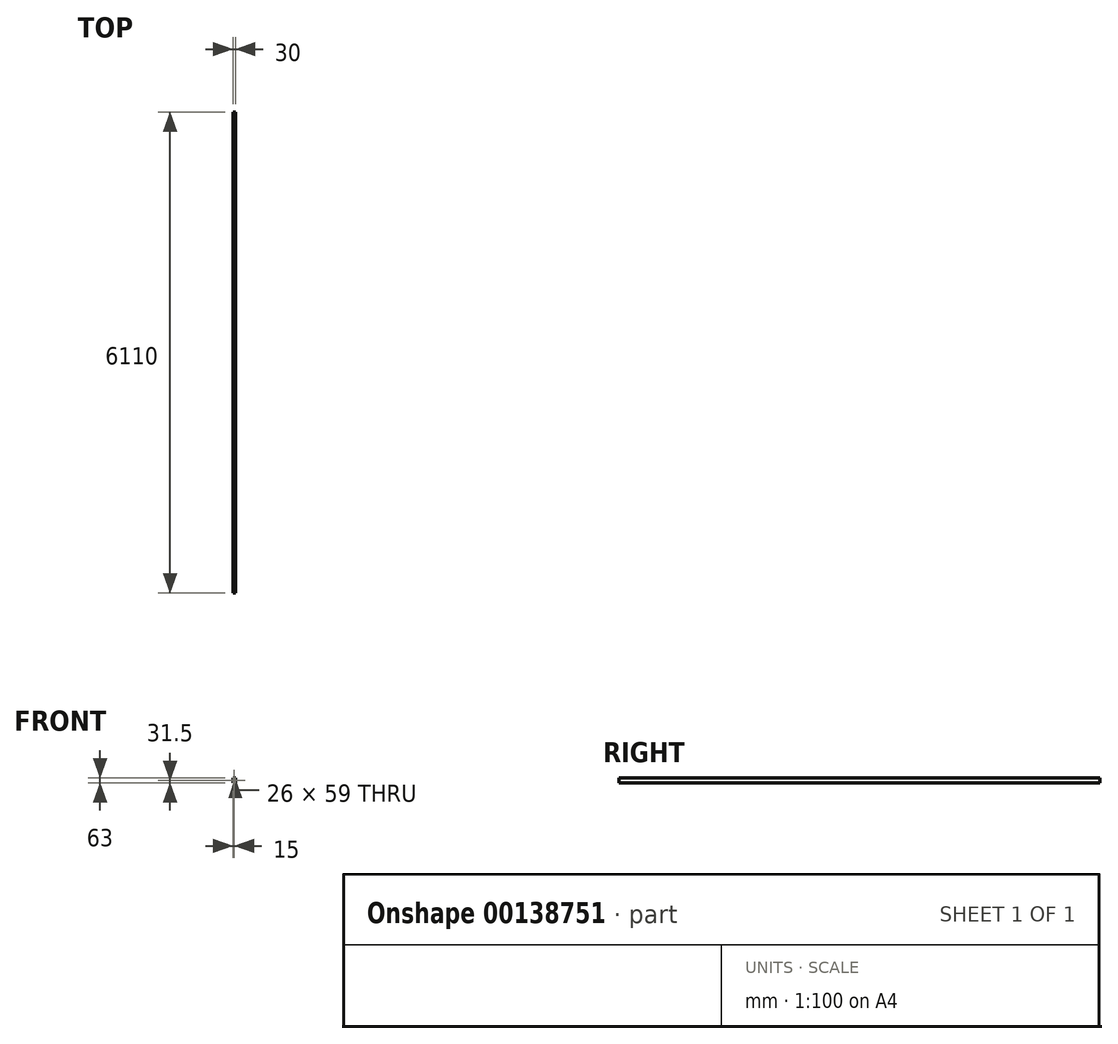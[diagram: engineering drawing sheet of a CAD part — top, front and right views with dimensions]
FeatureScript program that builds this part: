
annotation { "Feature Type Name" : "Feature", "Feature Type Description" : "" }
export const myFeature = defineFeature(function(context is Context, id is Id, definition is map)
    precondition{}
    {
        {
            var Q0;
            Q0=qCreatedBy(makeId("Front.planeOp"),FACE);
            var sketch = newSketch(context, id + "F0", { "sketchPlane" : qUnion([Q0])});
            skLineSegment(sketch, "E0.bottom", {"start": v(-15, 0) * mm, "end": v(15, 0) * mm});
            skLineSegment(sketch, "E0.top", {"start": v(-15, 63) * mm, "end": v(15, 63) * mm});
            skLineSegment(sketch, "E0.left", {"start": v(-15, 0) * mm, "end": v(-15, 63) * mm});
            skLineSegment(sketch, "E0.right", {"start": v(15, 0) * mm, "end": v(15, 63) * mm});
            skLineSegment(sketch, "E1.bottom", {"start": v(-13, 61) * mm, "end": v(13, 61) * mm});
            skLineSegment(sketch, "E1.top", {"start": v(-13, 2) * mm, "end": v(13, 2) * mm});
            skLineSegment(sketch, "E1.left", {"start": v(-13, 61) * mm, "end": v(-13, 2) * mm});
            skLineSegment(sketch, "E1.right", {"start": v(13, 61) * mm, "end": v(13, 2) * mm});
            skSolve(sketch);
        }
        {
            var Q0;
            Q0=qSketchRegion(id+"F0",true);
            extrude(context, id + "F1", {"entities" : qUnion([Q0]), "endBound" : BoundingType.SYMMETRIC, "depth" : 6110 * mm});
        }
    });
